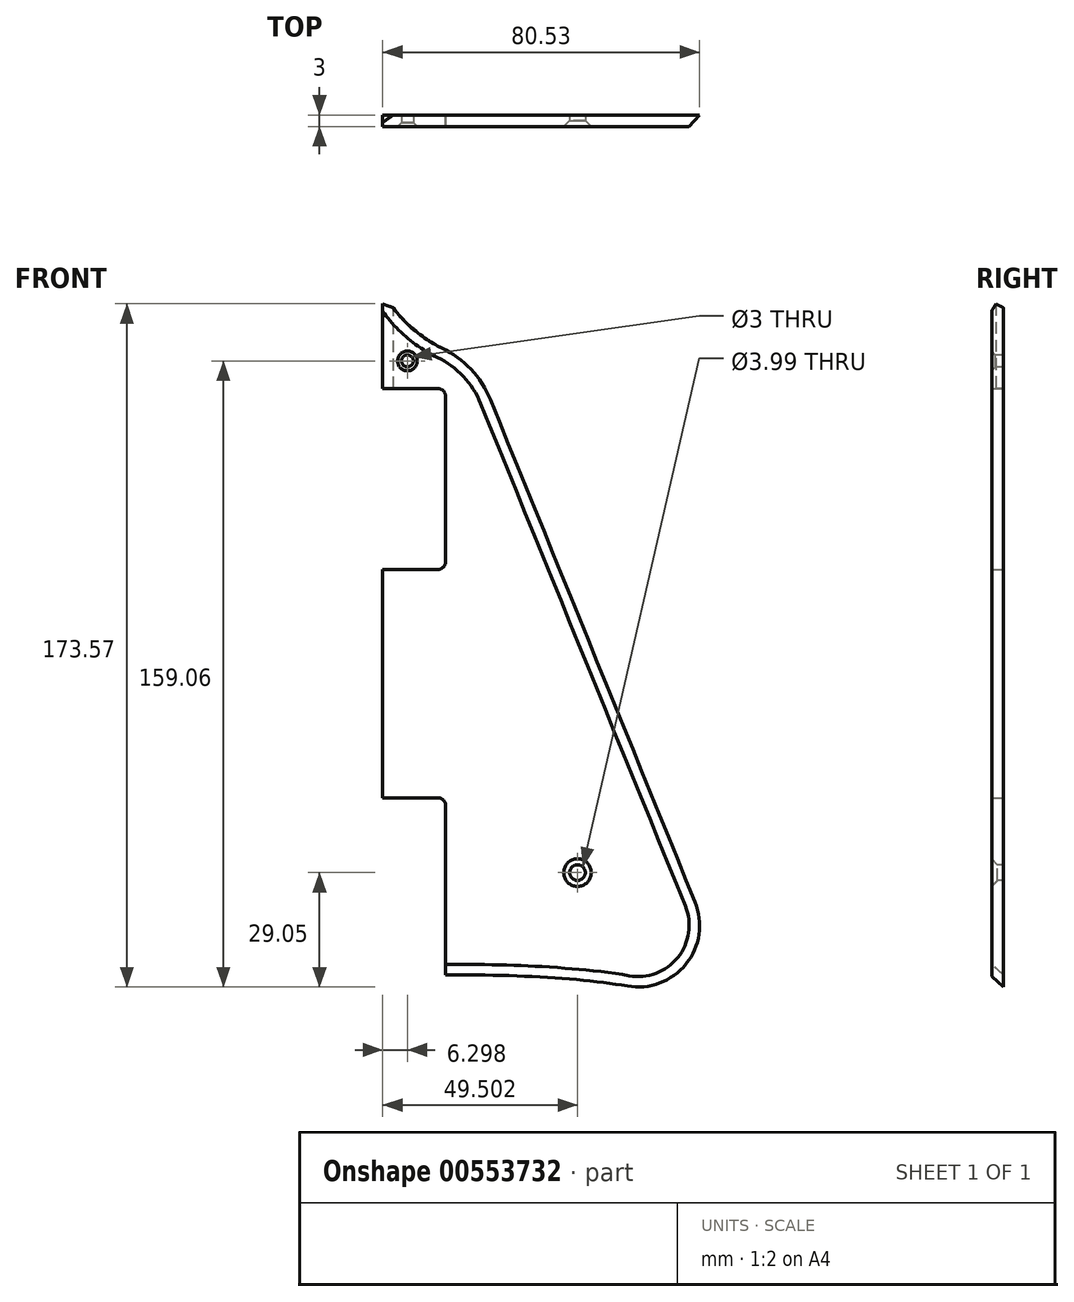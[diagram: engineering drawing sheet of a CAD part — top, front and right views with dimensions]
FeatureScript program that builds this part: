
annotation { "Feature Type Name" : "Feature", "Feature Type Description" : "" }
export const myFeature = defineFeature(function(context is Context, id is Id, definition is map)
    precondition{}
    {
        {
            var Q0;
            Q0=qCreatedBy(makeId("Front.planeOp"),FACE);
            var sketch = newSketch(context, id + "F0", { "sketchPlane" : qUnion([Q0])});
            skLineSegment(sketch, "E0", {"start": v(-23.07, 71) * mm, "end": v(-23.07, 46) * mm});
            skLineSegment(sketch, "E1", {"start": v(-23.07, 46) * mm, "end": v(-9.07, 46) * mm});
            skLineSegment(sketch, "E2", {"start": v(-9.08, 0) * mm, "end": v(-23.07, 0) * mm});
            skLineSegment(sketch, "E3", {"start": v(-23.07, 0) * mm, "end": v(-23.07, -58) * mm});
            skLineSegment(sketch, "E4", {"start": v(-23.07, -58) * mm, "end": v(-9.08, -58) * mm});
            skLineSegment(sketch, "E5", {"start": v(-7.07, -60) * mm, "end": v(-7.07, -102.98) * mm});
            skFitSpline(sketch, "E6", {"points": [v(-23.07, 71) * mm, v(-0.57, 55.29) * mm, v(0, 62.59) * mm], "startDerivative": vector(26.91, -56.87) * mm, "endDerivative": vector(28.21, 16.18) * mm});
            skLineSegment(sketch, "E7", {"start": v(-7.07, -102.98) * mm, "end": v(-3.07, -102.98) * mm});
            skFitSpline(sketch, "E8", {"points": [v(-3.07, -102.98) * mm, v(51.91, -115.4) * mm], "startDerivative": vector(96.06, 0) * mm, "endDerivative": vector(-29.84, -25.47) * mm});
            skPoint(sketch, "E9.visualSharp", {"position": v(78.9, -99.8) * mm});
            skPoint(sketch, "E10.visualSharp", {"position": v(-7.07, 0) * mm});
            skArc(sketch, "E11", {"start": v(39.1, -105.82) * mm, "mid": v(54, -100.22) * mm, "end": v(56.3, -84.48) * mm});
            skLineSegment(sketch, "E12", {"start": v(-7.07, 2) * mm, "end": v(-7.07, 44) * mm});
            skArc(sketch, "E13", {"start": v(-9.08, 0) * mm, "mid": v(-7.66, 0.59) * mm, "end": v(-7.07, 2) * mm});
            skArc(sketch, "E14", {"start": v(-9.07, 46) * mm, "mid": v(-7.66, 45.42) * mm, "end": v(-7.07, 44) * mm});
            skArc(sketch, "E15", {"start": v(-9.08, -58) * mm, "mid": v(-7.66, -58.59) * mm, "end": v(-7.07, -60) * mm});
            skFitSpline(sketch, "E16", {"points": [v(4.3, 43.17) * mm, v(56.3, -84.48) * mm], "startDerivative": vector(52, -127.59) * mm, "endDerivative": vector(52, -127.59) * mm});
            skArc(sketch, "E17", {"start": v(-8.03, 56.3) * mm, "mid": v(-0.64, 50.88) * mm, "end": v(4.3, 43.17) * mm});
            skPoint(sketch, "E18", {"position": v(-23.07, 58.5) * mm});
            skSolve(sketch);
        }
        {
            var Q0;
            Q0=makeQuery(id+"F0.imprint","IMPRINT",FACE,{"disambiguationData":[TD([[makeQuery(id+"F0.imprint","IMPRINT",EDGE,{"derivedFrom":sQuery(id+"F0.wireOp",EDGE,"E0")}),1.0]])]});
            var Q1;
            Q1 = qSketchRegion(id + "F3", true);
            extrude(context, id + "F1", {"entities" : qUnion([Q0, Q1]), "depth" : 3 * mm, "offsetDistance" : 25.4 * mm});
        }
        {
            var Q0;
            Q0=makeQuery(id+"F1.opExtrude","CAP_FACE",FACE,{"disambiguationData":[OSD([sQuery(id+"F0.wireOp",EDGE,"E0"),sQuery(id+"F0.wireOp",EDGE,"E1"),sQuery(id+"F0.wireOp",EDGE,"E2"),sQuery(id+"F0.wireOp",EDGE,"E3"),sQuery(id+"F0.wireOp",EDGE,"E4"),sQuery(id+"F0.wireOp",EDGE,"E5"),sQuery(id+"F0.wireOp",EDGE,"E6"),sQuery(id+"F0.wireOp",EDGE,"E7"),sQuery(id+"F0.wireOp",EDGE,"E8"),sQuery(id+"F0.wireOp",EDGE,"QMKCutLS-we9p-TS8p-Kuok-RDuJMA0QMHhA"),sQuery(id+"F0.wireOp",EDGE,"YVnC9wJ3-t3rX-aTt8-vZLE-TqHRbTgYmHF5"),sQuery(id+"F0.wireOp",EDGE,"E11"),sQuery(id+"F0.wireOp",EDGE,"E12"),sQuery(id+"F0.wireOp",EDGE,"E13"),sQuery(id+"F0.wireOp",EDGE,"E14"),sQuery(id+"F0.wireOp",EDGE,"E15"),sQuery(id+"F0.wireOp",EDGE,"4dba2c9f-f87c-456e-b8df-559161210a71")])],"isStart":false});
            var sketch = newSketch(context, id + "F2", { "sketchPlane" : qUnion([Q0])});
            skCircle(sketch, "E19", {"center": v(26.43, -77) * mm, "radius": 2 * mm});
            skSolve(sketch);
        }
        {
            var Q0;
            Q0=makeQuery(id+"F2.imprint","IMPRINT",FACE,{"disambiguationData":[TD([[makeQuery(id+"F2.imprint","IMPRINT",EDGE,{"derivedFrom":sQuery(id+"F2.wireOp",EDGE,"E19")}),-1.0]])]});
            var sketch = newSketch(context, id + "F3", { "sketchPlane" : qUnion([Q0])});
            skCircle(sketch, "E20", {"center": v(-16.77, 53.01) * mm, "radius": 1.5 * mm});
            skSolve(sketch);
        }
        {
            var Q0;
            Q0=sQuery(id+"F3.wireOp",VERTEX,"E20.center");
            var Q1;
            Q1=makeQuery(id+"F1.opExtrude","SWEPT_BODY",BODY,{"disambiguationData":[OSD([sQuery(id+"F0.wireOp",EDGE,"E0"),sQuery(id+"F0.wireOp",EDGE,"E1"),sQuery(id+"F0.wireOp",EDGE,"E2"),sQuery(id+"F0.wireOp",EDGE,"E3"),sQuery(id+"F0.wireOp",EDGE,"E4"),sQuery(id+"F0.wireOp",EDGE,"E5"),sQuery(id+"F0.wireOp",EDGE,"E6"),sQuery(id+"F0.wireOp",EDGE,"E7"),sQuery(id+"F0.wireOp",EDGE,"E8"),sQuery(id+"F0.wireOp",EDGE,"E11"),sQuery(id+"F0.wireOp",EDGE,"E12"),sQuery(id+"F0.wireOp",EDGE,"E13"),sQuery(id+"F0.wireOp",EDGE,"E14"),sQuery(id+"F0.wireOp",EDGE,"E15"),sQuery(id+"F0.wireOp",EDGE,"E16"),sQuery(id+"F0.wireOp",EDGE,"E17")])]});
            hole(context, id + "F4", {"style" : HoleStyle.C_SINK, "endStyle" : HoleEndStyle.THROUGH, "holeDiameter" : 3 * mm, "cSinkDiameter" : 5 * mm, "cSinkAngle" : 90 * degree, "isTappedThrough" : true, "tappedDepth" : 12.7 * mm, "tapClearance" : 3, "locations" : qUnion([Q0]), "scope" : qUnion([Q1])});
        }
        {
            var Q0;
            Q0=sQuery(id+"F2.wireOp",VERTEX,"E19.center");
            var Q1;
            Q1=makeQuery(id+"F1.opExtrude","SWEPT_BODY",BODY,{"disambiguationData":[OSD([sQuery(id+"F0.wireOp",EDGE,"E0"),sQuery(id+"F0.wireOp",EDGE,"E1"),sQuery(id+"F0.wireOp",EDGE,"E2"),sQuery(id+"F0.wireOp",EDGE,"E3"),sQuery(id+"F0.wireOp",EDGE,"E4"),sQuery(id+"F0.wireOp",EDGE,"E5"),sQuery(id+"F0.wireOp",EDGE,"E6"),sQuery(id+"F0.wireOp",EDGE,"E7"),sQuery(id+"F0.wireOp",EDGE,"E8"),sQuery(id+"F0.wireOp",EDGE,"E11"),sQuery(id+"F0.wireOp",EDGE,"E12"),sQuery(id+"F0.wireOp",EDGE,"E13"),sQuery(id+"F0.wireOp",EDGE,"E14"),sQuery(id+"F0.wireOp",EDGE,"E15"),sQuery(id+"F0.wireOp",EDGE,"E16"),sQuery(id+"F0.wireOp",EDGE,"E17")])]});
            hole(context, id + "F5", {"style" : HoleStyle.C_SINK, "endStyle" : HoleEndStyle.THROUGH, "holeDiameter" : 4 * mm, "cSinkDiameter" : 7 * mm, "cSinkAngle" : 90 * degree, "isTappedThrough" : true, "tappedDepth" : 12.7 * mm, "tapClearance" : 3, "locations" : qUnion([Q0]), "scope" : qUnion([Q1])});
        }
        {
            var Q0;
            Q0=makeQuery(id+"F1.opExtrude","CAP_EDGE",EDGE,{"disambiguationData":[OSD([sQuery(id+"F0.wireOp",EDGE,"E16")])],"isStart":false});
            chamfer(context, id + "F6", {"entities" : qUnion([Q0]), "chamferType" : ChamferType.OFFSET_ANGLE, "width" : 2.95 * mm, "oppositeDirection" : false, "angle" : 42 * degree, "tangentPropagation" : true});
        }
        {
            var Q0;
            Q0=makeQuery(id+"F1.opExtrude","CAP_EDGE",EDGE,{"disambiguationData":[OSD([sQuery(id+"F0.wireOp",EDGE,"E0")])],"isStart":true});
            chamfer(context, id + "F7", {"entities" : qUnion([Q0]), "chamferType" : ChamferType.OFFSET_ANGLE, "width" : 1.9 * mm, "oppositeDirection" : false, "angle" : 55 * degree, "tangentPropagation" : true});
        }
    });
